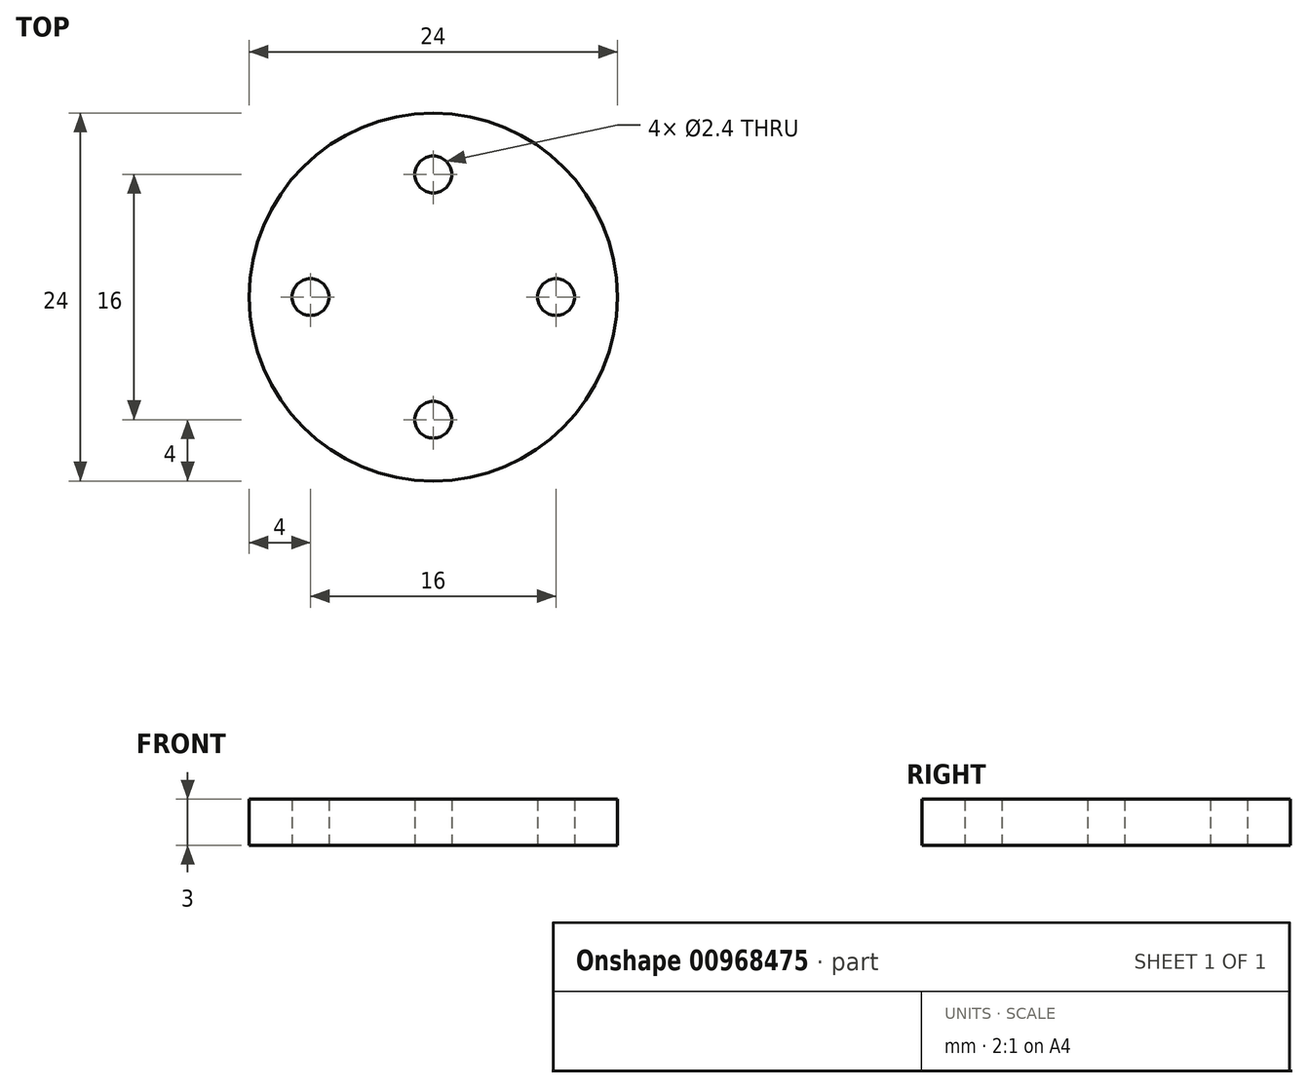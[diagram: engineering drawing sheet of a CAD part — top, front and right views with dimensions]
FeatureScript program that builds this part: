
annotation { "Feature Type Name" : "Feature", "Feature Type Description" : "" }
export const myFeature = defineFeature(function(context is Context, id is Id, definition is map)
    precondition{}
    {
        {
            var Q0;
            Q0=qCreatedBy(makeId("Top.planeOp"),FACE);
            var sketch = newSketch(context, id + "F0", { "sketchPlane" : qUnion([Q0])});
            skCircle(sketch, "E0", {"center": v(0, 0) * mm, "radius": 12 * mm});
            skCircle(sketch, "E1", {"center": v(0, 0) * mm, "radius": 8 * mm, "construction": true});
            skCircle(sketch, "E2", {"center": v(0, -8) * mm, "radius": 1.2 * mm});
            skCircle(sketch, "E3.1.0", {"center": v(8, 0) * mm, "radius": 1.2 * mm});
            skCircle(sketch, "E3.2.0", {"center": v(0, 8) * mm, "radius": 1.2 * mm});
            skCircle(sketch, "E3.3.0", {"center": v(-8, 0) * mm, "radius": 1.2 * mm});
            skSolve(sketch);
        }
        {
            var Q0;
            Q0 = qSketchRegion(id + "F0", true);
            extrude(context, id + "F1", {"entities" : qUnion([Q0]), "depth" : 3 * mm, "offsetDistance" : 25 * mm});
        }
    });
